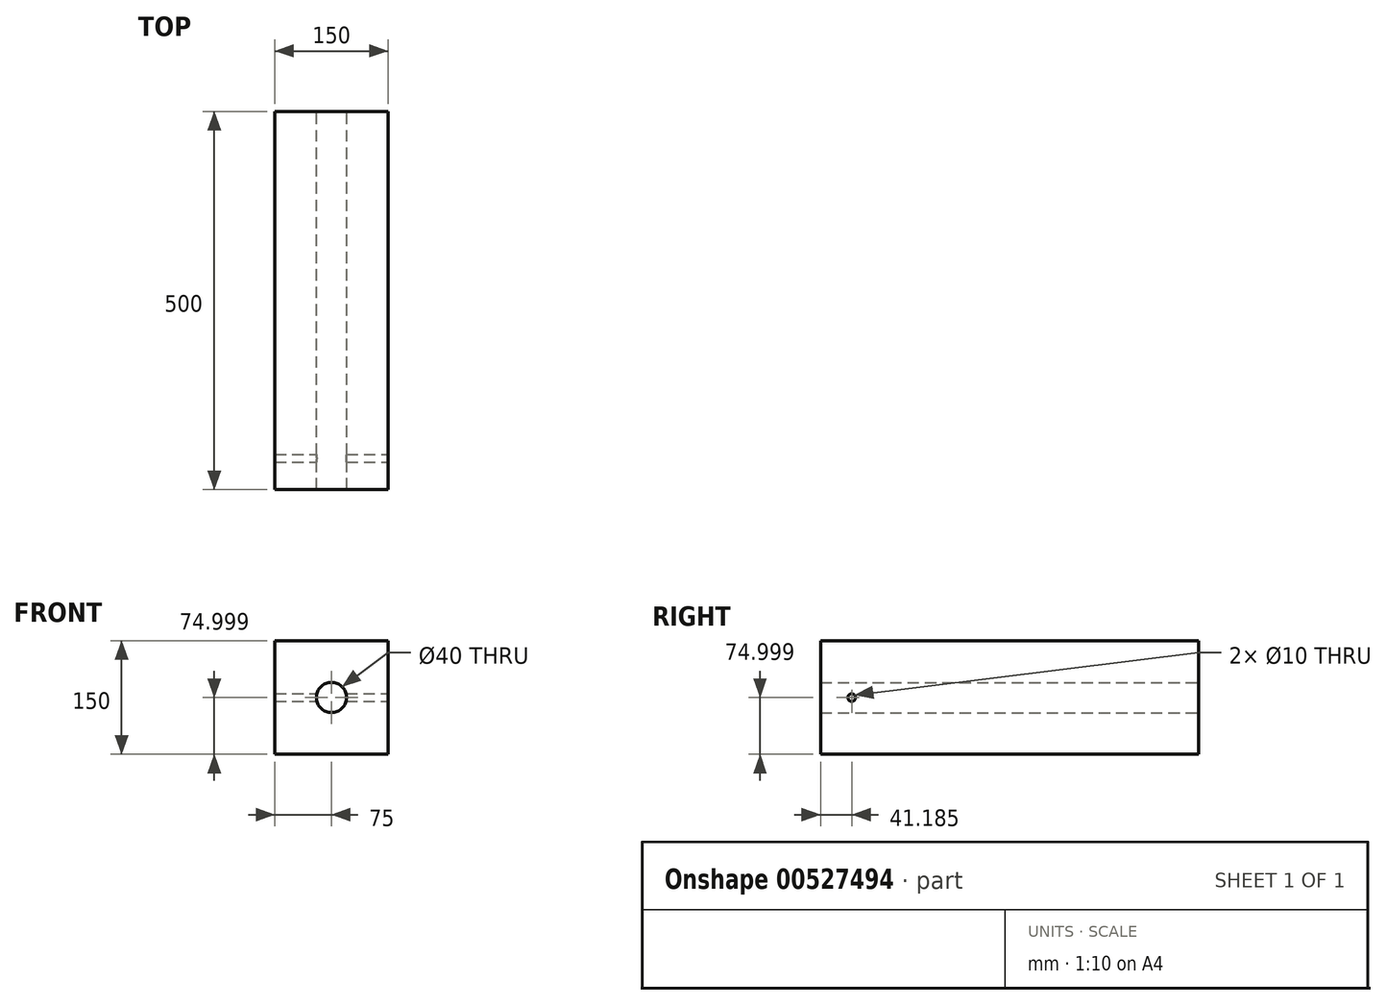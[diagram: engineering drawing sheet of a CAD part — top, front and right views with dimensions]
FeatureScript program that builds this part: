
annotation { "Feature Type Name" : "Feature", "Feature Type Description" : "" }
export const myFeature = defineFeature(function(context is Context, id is Id, definition is map)
    precondition{}
    {
        {
            var Q0;
            Q0=qCreatedBy(makeId("Front.planeOp"),FACE);
            var sketch = newSketch(context, id + "F0", { "sketchPlane" : qUnion([Q0])});
            skLineSegment(sketch, "E0.bottom", {"start": v(78.68, 99.78) * mm, "end": v(-71.32, 99.78) * mm});
            skLineSegment(sketch, "E0.top", {"start": v(78.68, -50.22) * mm, "end": v(-71.32, -50.22) * mm});
            skLineSegment(sketch, "E0.left", {"start": v(78.68, 99.78) * mm, "end": v(78.68, -50.22) * mm});
            skLineSegment(sketch, "E0.right", {"start": v(-71.32, 99.78) * mm, "end": v(-71.32, -50.22) * mm});
            skLineSegment(sketch, "E1", {"start": v(3.68, 99.78) * mm, "end": v(3.68, -50.22) * mm, "construction": true});
            skLineSegment(sketch, "E2", {"start": v(3.68, -50.22) * mm, "end": v(78.68, 24.78) * mm, "construction": true});
            skLineSegment(sketch, "E3", {"start": v(78.68, 24.78) * mm, "end": v(-71.32, 24.78) * mm, "construction": true});
            skCircle(sketch, "E4", {"center": v(3.68, 24.78) * mm, "radius": 20 * mm});
            skSolve(sketch);
        }
        {
            var Q0;
            Q0 = qSketchRegion(id + "F0", true);
            extrude(context, id + "F1", {"entities" : qUnion([Q0]), "depth" : 500 * mm, "offsetDistance" : 25 * mm});
        }
        {
            var Q0;
            Q0=makeQuery(id+"F1.opExtrude","SWEPT_FACE",FACE,{"disambiguationData":[OSD([sQuery(id+"F0.wireOp",EDGE,"E0.left")])]});
            var sketch = newSketch(context, id + "F2", { "sketchPlane" : qUnion([Q0])});
            skPoint(sketch, "E5", {"position": v(-458.82, 24.78) * mm});
            skPoint(sketch, "E5.positionSnap0", {"position": v(-500, 24.78) * mm});
            skSolve(sketch);
        }
        {
            var Q0;
            Q0=sQuery(id+"F2.wireOp",VERTEX,"E5");
            var Q1;
            Q1=makeQuery(id+"F1.opExtrude","SWEPT_BODY",BODY,{"disambiguationData":[OSD([sQuery(id+"F0.wireOp",EDGE,"E0.bottom"),sQuery(id+"F0.wireOp",EDGE,"E0.top"),sQuery(id+"F0.wireOp",EDGE,"E0.left"),sQuery(id+"F0.wireOp",EDGE,"E0.right"),sQuery(id+"F0.wireOp",EDGE,"E4")])]});
            hole(context, id + "F3", {"style" : HoleStyle.SIMPLE, "endStyle" : HoleEndStyle.THROUGH, "holeDiameter" : 10 * mm, "isTappedThrough" : true, "tappedDepth" : 12 * mm, "tapClearance" : 3, "startFromSketch" : true, "locations" : qUnion([Q0]), "scope" : qUnion([Q1])});
        }
    });
